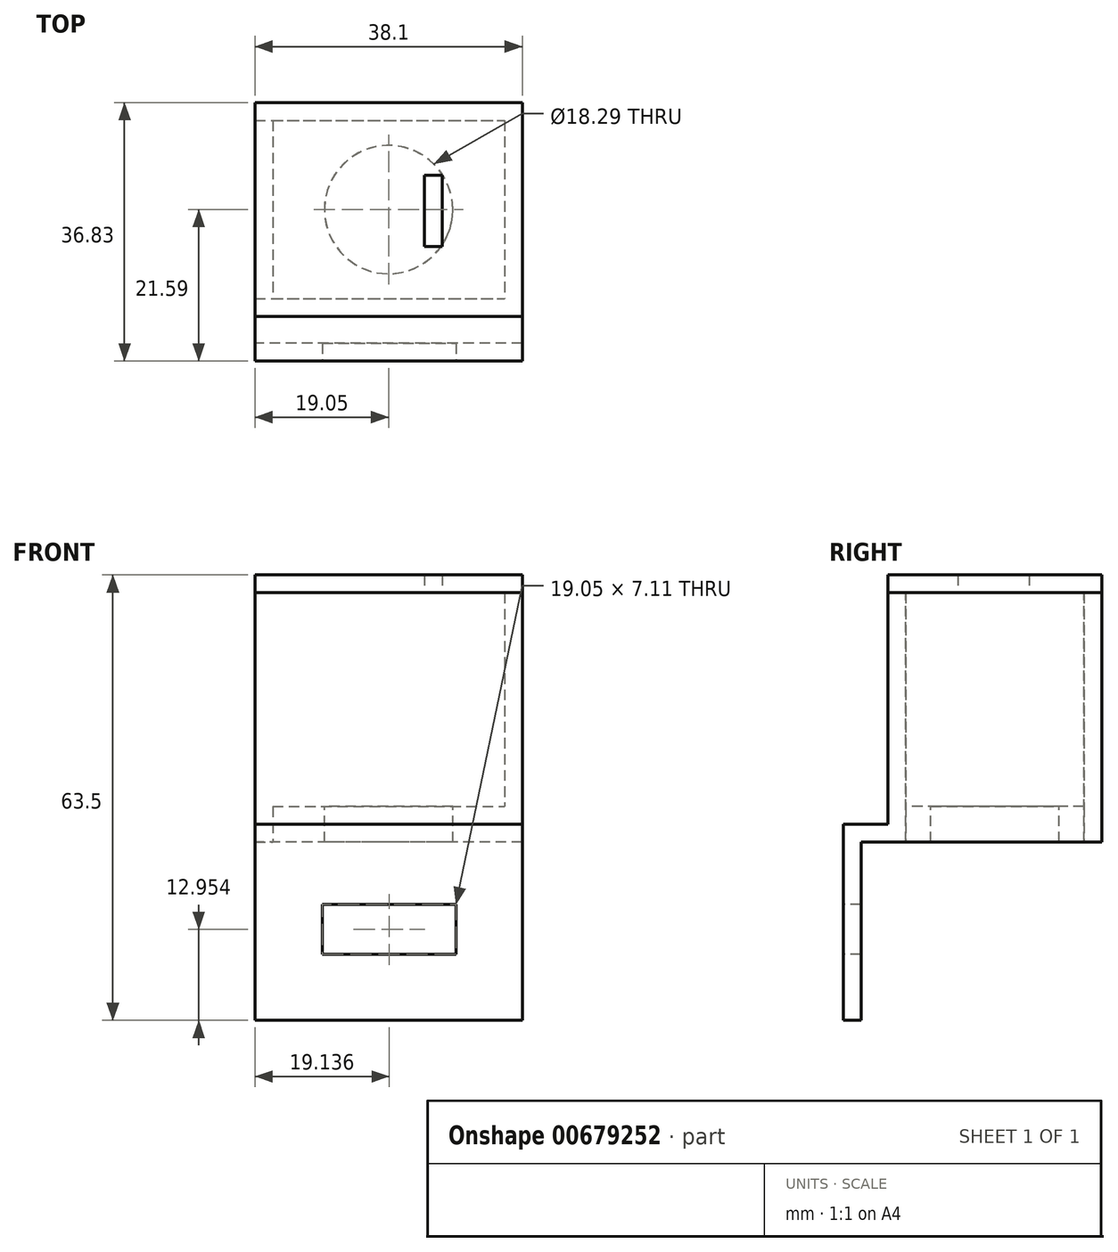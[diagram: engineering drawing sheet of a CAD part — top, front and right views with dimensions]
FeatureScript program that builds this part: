
annotation { "Feature Type Name" : "Feature", "Feature Type Description" : "" }
export const myFeature = defineFeature(function(context is Context, id is Id, definition is map)
    precondition{}
    {
        {
            var Q0;
            Q0=qCreatedBy(makeId("Top.planeOp"),FACE);
            var sketch = newSketch(context, id + "F0", { "sketchPlane" : qUnion([Q0])});
            skLineSegment(sketch, "E0.bottom", {"start": v(0, 25.4) * mm, "end": v(33.02, 25.4) * mm});
            skLineSegment(sketch, "E0.top", {"start": v(0, 0) * mm, "end": v(33.02, 0) * mm});
            skLineSegment(sketch, "E0.left", {"start": v(0, 25.4) * mm, "end": v(0, 0) * mm});
            skLineSegment(sketch, "E0.right", {"start": v(33.02, 25.4) * mm, "end": v(33.02, 0) * mm});
            skSolve(sketch);
        }
        {
            var Q0;
            Q0=makeQuery(id+"F0.imprint","IMPRINT",FACE,{"disambiguationData":[TD([[makeQuery(id+"F0.imprint","IMPRINT",EDGE,{"derivedFrom":sQuery(id+"F0.wireOp",EDGE,"E0.bottom")}),-1.0]])]});
            extrude(context, id + "F1", {"entities" : qUnion([Q0]), "depth" : 5.08 * mm, "offsetDistance" : 25.4 * mm});
        }
        {
            var Q0;
            Q0=makeQuery(id+"F1.opExtrude","CAP_FACE",FACE,{"disambiguationData":[OSD([sQuery(id+"F0.wireOp",EDGE,"E0.bottom"),sQuery(id+"F0.wireOp",EDGE,"E0.top"),sQuery(id+"F0.wireOp",EDGE,"E0.left"),sQuery(id+"F0.wireOp",EDGE,"E0.right")])],"isStart":false});
            var sketch = newSketch(context, id + "F2", { "sketchPlane" : qUnion([Q0])});
            skCircle(sketch, "E1", {"center": v(16.51, 12.7) * mm, "radius": 9.14 * mm});
            skSolve(sketch);
        }
        {
            var Q0;
            Q0=makeQuery(id+"F2.imprint","IMPRINT",FACE,{"disambiguationData":[TD([[makeQuery(id+"F2.imprint","IMPRINT",EDGE,{"derivedFrom":sQuery(id+"F2.wireOp",EDGE,"E1")}),1.0]])]});
            extrude(context, id + "F3", {"entities" : qUnion([Q0]), "operationType" : NewBodyOperationType.REMOVE, "endBound" : BoundingType.THROUGH_ALL, "oppositeDirection" : true, "depth" : 25.4 * mm, "offsetDistance" : 25.4 * mm});
        }
        {
            var Q0;
            Q0=qCreatedBy(makeId("Front.planeOp"),FACE);
            var sketch = newSketch(context, id + "F4", { "sketchPlane" : qUnion([Q0])});
            skLineSegment(sketch, "E2.bottom", {"start": v(-2.54, 0) * mm, "end": v(35.56, 0) * mm});
            skLineSegment(sketch, "E2.top", {"start": v(-2.54, 35.56) * mm, "end": v(35.56, 35.56) * mm});
            skLineSegment(sketch, "E2.left", {"start": v(-2.54, 0) * mm, "end": v(-2.54, 35.56) * mm});
            skLineSegment(sketch, "E2.right", {"start": v(35.56, 0) * mm, "end": v(35.56, 35.56) * mm});
            skSolve(sketch);
        }
        {
            var Q0;
            Q0=makeQuery(id+"F4.imprint","IMPRINT",FACE,{"disambiguationData":[TD([[makeQuery(id+"F4.imprint","IMPRINT",EDGE,{"derivedFrom":sQuery(id+"F4.wireOp",EDGE,"E2.bottom")}),1.0]])]});
            extrude(context, id + "F5", {"entities" : qUnion([Q0]), "operationType" : NewBodyOperationType.ADD, "depth" : 2.54 * mm, "offsetDistance" : 25.4 * mm});
        }
        {
            var Q0;
            Q0=makeQuery(id+"F1.opExtrude","SWEPT_FACE",FACE,{"disambiguationData":[OSD([sQuery(id+"F0.wireOp",EDGE,"E0.bottom")])]});
            var sketch = newSketch(context, id + "F6", { "sketchPlane" : qUnion([Q0])});
            skLineSegment(sketch, "E3.bottom", {"start": v(2.54, 0) * mm, "end": v(-35.56, 0) * mm});
            skLineSegment(sketch, "E3.top", {"start": v(2.54, 35.56) * mm, "end": v(-35.56, 35.56) * mm});
            skLineSegment(sketch, "E3.left", {"start": v(2.54, 0) * mm, "end": v(2.54, 35.56) * mm});
            skLineSegment(sketch, "E3.right", {"start": v(-35.56, 0) * mm, "end": v(-35.56, 35.56) * mm});
            skSolve(sketch);
        }
        {
            var Q0;
            Q0 = qSketchRegion(id + "F6", true);
            extrude(context, id + "F7", {"entities" : qUnion([Q0]), "operationType" : NewBodyOperationType.ADD, "depth" : 2.54 * mm, "offsetDistance" : 25.4 * mm});
        }
        {
            var Q0;
            Q0=makeQuery(id+"F7.opExtrude","CAP_FACE",FACE,{"disambiguationData":[OSD([sQuery(id+"F6.wireOp",EDGE,"E3.bottom"),sQuery(id+"F6.wireOp",EDGE,"E3.top"),sQuery(id+"F6.wireOp",EDGE,"E3.left"),sQuery(id+"F6.wireOp",EDGE,"E3.right")])],"isStart":true});
            var sketch = newSketch(context, id + "F8", { "sketchPlane" : qUnion([Q0])});
            skLineSegment(sketch, "E4.bottom", {"start": v(35.56, 35.56) * mm, "end": v(33.02, 35.56) * mm});
            skLineSegment(sketch, "E4.top", {"start": v(35.56, 0) * mm, "end": v(33.02, 0) * mm});
            skLineSegment(sketch, "E4.left", {"start": v(35.56, 35.56) * mm, "end": v(35.56, 0) * mm});
            skLineSegment(sketch, "E4.right", {"start": v(33.02, 35.56) * mm, "end": v(33.02, 0) * mm});
            skSolve(sketch);
        }
        {
            var Q0;
            {var subQ2=sQuery(id+"F8.wireOp",EDGE,"E4.bottom");Q0=makeQuery(id+"F8.imprint","IMPRINT",FACE,{"disambiguationData":[TD([[makeQuery(id+"F8.imprint","IMPRINT",EDGE,{"derivedFrom":subQ2}),-1.0]])]});}
            var Q1;
            Q1=makeQuery(id+"F5.opExtrude","CAP_FACE",FACE,{"disambiguationData":[OSD([sQuery(id+"F4.wireOp",EDGE,"E2.bottom"),sQuery(id+"F4.wireOp",EDGE,"E2.top"),sQuery(id+"F4.wireOp",EDGE,"E2.left"),sQuery(id+"F4.wireOp",EDGE,"E2.right")])],"isStart":true});
            extrude(context, id + "F9", {"entities" : qUnion([Q0]), "operationType" : NewBodyOperationType.ADD, "endBound" : BoundingType.UP_TO_SURFACE, "depth" : 25.4 * mm, "endBoundEntityFace" : qUnion([Q1]), "offsetDistance" : 25.4 * mm});
        }
        {
            var Q0;
            Q0=makeQuery(id+"F9.boolean.opBoolean","MERGE",FACE,{"derivedFrom":[makeQuery(id+"F5.opExtrude","SWEPT_FACE",FACE,{"disambiguationData":[OSD([sQuery(id+"F4.wireOp",EDGE,"E2.top")])]}),makeQuery(id+"F7.opExtrude","SWEPT_FACE",FACE,{"disambiguationData":[OSD([sQuery(id+"F6.wireOp",EDGE,"E3.top")])]}),makeQuery(id+"F9.opExtrude","SWEPT_FACE",FACE,{"disambiguationData":[OSD([sQuery(id+"F8.wireOp",EDGE,"E4.bottom")])]})]});
            var sketch = newSketch(context, id + "F10", { "sketchPlane" : qUnion([Q0])});
            skLineSegment(sketch, "E5.bottom", {"start": v(35.56, 27.94) * mm, "end": v(-2.54, 27.94) * mm});
            skLineSegment(sketch, "E5.top", {"start": v(35.56, -2.54) * mm, "end": v(-2.54, -2.54) * mm});
            skLineSegment(sketch, "E5.left", {"start": v(35.56, 27.94) * mm, "end": v(35.56, -2.54) * mm});
            skLineSegment(sketch, "E5.right", {"start": v(-2.54, 27.94) * mm, "end": v(-2.54, -2.54) * mm});
            skLineSegment(sketch, "E6.bottom", {"start": v(24.13, 17.6) * mm, "end": v(21.6, 17.6) * mm});
            skLineSegment(sketch, "E6.top", {"start": v(24.13, 7.44) * mm, "end": v(21.6, 7.44) * mm});
            skLineSegment(sketch, "E6.left", {"start": v(24.13, 17.6) * mm, "end": v(24.13, 7.44) * mm});
            skLineSegment(sketch, "E6.right", {"start": v(21.6, 17.6) * mm, "end": v(21.6, 7.44) * mm});
            skSolve(sketch);
        }
        {
            var Q0;
            Q0=makeQuery(id+"F10.imprint","IMPRINT",FACE,{"disambiguationData":[TD([[makeQuery(id+"F10.imprint","IMPRINT",EDGE,{"derivedFrom":sQuery(id+"F10.wireOp",EDGE,"E6.bottom")}),-1.0]])]});
            var Q1;
            {var subQ5=sQuery(id+"F10.wireOp",EDGE,"E5.bottom");Q1=makeQuery(id+"F10.imprint","IMPRINT",FACE,{"disambiguationData":[TD([[makeQuery(id+"F10.imprint","IMPRINT",EDGE,{"derivedFrom":subQ5}),-1.0]])]});}
            extrude(context, id + "F11", {"entities" : qUnion([Q0, Q1]), "depth" : 2.54 * mm, "offsetDistance" : 25.4 * mm});
        }
        {
            var Q0;
            Q0=makeQuery(id+"F5.opExtrude","CAP_FACE",FACE,{"disambiguationData":[OSD([sQuery(id+"F4.wireOp",EDGE,"E2.bottom"),sQuery(id+"F4.wireOp",EDGE,"E2.top"),sQuery(id+"F4.wireOp",EDGE,"E2.left"),sQuery(id+"F4.wireOp",EDGE,"E2.right")])],"isStart":false});
            var sketch = newSketch(context, id + "F12", { "sketchPlane" : qUnion([Q0])});
            skLineSegment(sketch, "E7.bottom", {"start": v(35.56, 0) * mm, "end": v(-2.54, 0) * mm});
            skLineSegment(sketch, "E7.top", {"start": v(35.56, 2.54) * mm, "end": v(-2.54, 2.54) * mm});
            skLineSegment(sketch, "E7.left", {"start": v(35.56, 0) * mm, "end": v(35.56, 2.54) * mm});
            skLineSegment(sketch, "E7.right", {"start": v(-2.54, 0) * mm, "end": v(-2.54, 2.54) * mm});
            skSolve(sketch);
        }
        {
            var Q0;
            Q0=makeQuery(id+"F12.imprint","IMPRINT",FACE,{"disambiguationData":[TD([[makeQuery(id+"F12.imprint","IMPRINT",EDGE,{"derivedFrom":sQuery(id+"F12.wireOp",EDGE,"E7.bottom")}),1.0]])]});
            extrude(context, id + "F13", {"entities" : qUnion([Q0]), "operationType" : NewBodyOperationType.ADD, "depth" : 6.35 * mm, "offsetDistance" : 25.4 * mm});
        }
        {
            var Q0;
            Q0=makeQuery(id+"F13.boolean.opBoolean","MERGE",FACE,{"derivedFrom":[makeQuery(id+"F9.boolean.opBoolean","MERGE",FACE,{"derivedFrom":[makeQuery(id+"F7.boolean.opBoolean","MERGE",FACE,{"derivedFrom":[makeQuery(id+"F5.boolean.opBoolean","MERGE",FACE,{"derivedFrom":[makeQuery(id+"F1.opExtrude","CAP_FACE",FACE,{"disambiguationData":[OSD([sQuery(id+"F0.wireOp",EDGE,"E0.bottom"),sQuery(id+"F0.wireOp",EDGE,"E0.top"),sQuery(id+"F0.wireOp",EDGE,"E0.left"),sQuery(id+"F0.wireOp",EDGE,"E0.right")])],"isStart":true}),makeQuery(id+"F5.opExtrude","SWEPT_FACE",FACE,{"disambiguationData":[OSD([sQuery(id+"F4.wireOp",EDGE,"E2.bottom")])]})]}),makeQuery(id+"F7.opExtrude","SWEPT_FACE",FACE,{"disambiguationData":[OSD([sQuery(id+"F6.wireOp",EDGE,"E3.bottom")])]})]}),makeQuery(id+"F9.opExtrude","SWEPT_FACE",FACE,{"disambiguationData":[OSD([sQuery(id+"F8.wireOp",EDGE,"E4.top")])]})]}),makeQuery(id+"F13.opExtrude","SWEPT_FACE",FACE,{"disambiguationData":[OSD([sQuery(id+"F12.wireOp",EDGE,"E7.bottom")])]})]});
            var sketch = newSketch(context, id + "F14", { "sketchPlane" : qUnion([Q0])});
            skLineSegment(sketch, "E8.bottom", {"start": v(35.56, 8.9) * mm, "end": v(-2.54, 8.9) * mm});
            skLineSegment(sketch, "E8.top", {"start": v(35.56, 6.35) * mm, "end": v(-2.54, 6.35) * mm});
            skLineSegment(sketch, "E8.left", {"start": v(35.56, 8.9) * mm, "end": v(35.56, 6.35) * mm});
            skLineSegment(sketch, "E8.right", {"start": v(-2.54, 8.9) * mm, "end": v(-2.54, 6.35) * mm});
            skSolve(sketch);
        }
        {
            var Q0;
            Q0=makeQuery(id+"F14.imprint","IMPRINT",FACE,{"disambiguationData":[TD([[makeQuery(id+"F14.imprint","IMPRINT",EDGE,{"derivedFrom":sQuery(id+"F14.wireOp",EDGE,"E8.bottom")}),-1.0]])]});
            extrude(context, id + "F15", {"entities" : qUnion([Q0]), "operationType" : NewBodyOperationType.ADD, "depth" : 25.4 * mm, "offsetDistance" : 25.4 * mm});
        }
        {
            var Q0;
            Q0=makeQuery(id+"F15.boolean.opBoolean","MERGE",FACE,{"derivedFrom":[makeQuery(id+"F13.opExtrude","CAP_FACE",FACE,{"disambiguationData":[OSD([sQuery(id+"F12.wireOp",EDGE,"E7.bottom"),sQuery(id+"F12.wireOp",EDGE,"E7.top"),sQuery(id+"F12.wireOp",EDGE,"E7.left"),sQuery(id+"F12.wireOp",EDGE,"E7.right")])],"isStart":false}),makeQuery(id+"F15.opExtrude","SWEPT_FACE",FACE,{"disambiguationData":[OSD([sQuery(id+"F14.wireOp",EDGE,"E8.bottom")])]})]});
            var sketch = newSketch(context, id + "F16", { "sketchPlane" : qUnion([Q0])});
            skLineSegment(sketch, "E9.bottom", {"start": v(26.12, -8.9) * mm, "end": v(7.07, -8.9) * mm});
            skLineSegment(sketch, "E9.top", {"start": v(26.12, -16) * mm, "end": v(7.07, -16) * mm});
            skLineSegment(sketch, "E9.left", {"start": v(26.12, -8.9) * mm, "end": v(26.12, -16) * mm});
            skLineSegment(sketch, "E9.right", {"start": v(7.07, -8.9) * mm, "end": v(7.07, -16) * mm});
            skSolve(sketch);
        }
        {
            var Q0;
            Q0=makeQuery(id+"F16.imprint","IMPRINT",FACE,{"disambiguationData":[TD([[makeQuery(id+"F16.imprint","IMPRINT",EDGE,{"derivedFrom":sQuery(id+"F16.wireOp",EDGE,"E9.bottom")}),1.0]])]});
            extrude(context, id + "F17", {"entities" : qUnion([Q0]), "operationType" : NewBodyOperationType.REMOVE, "oppositeDirection" : true, "depth" : 25.4 * mm, "offsetDistance" : 25.4 * mm});
        }
    });
